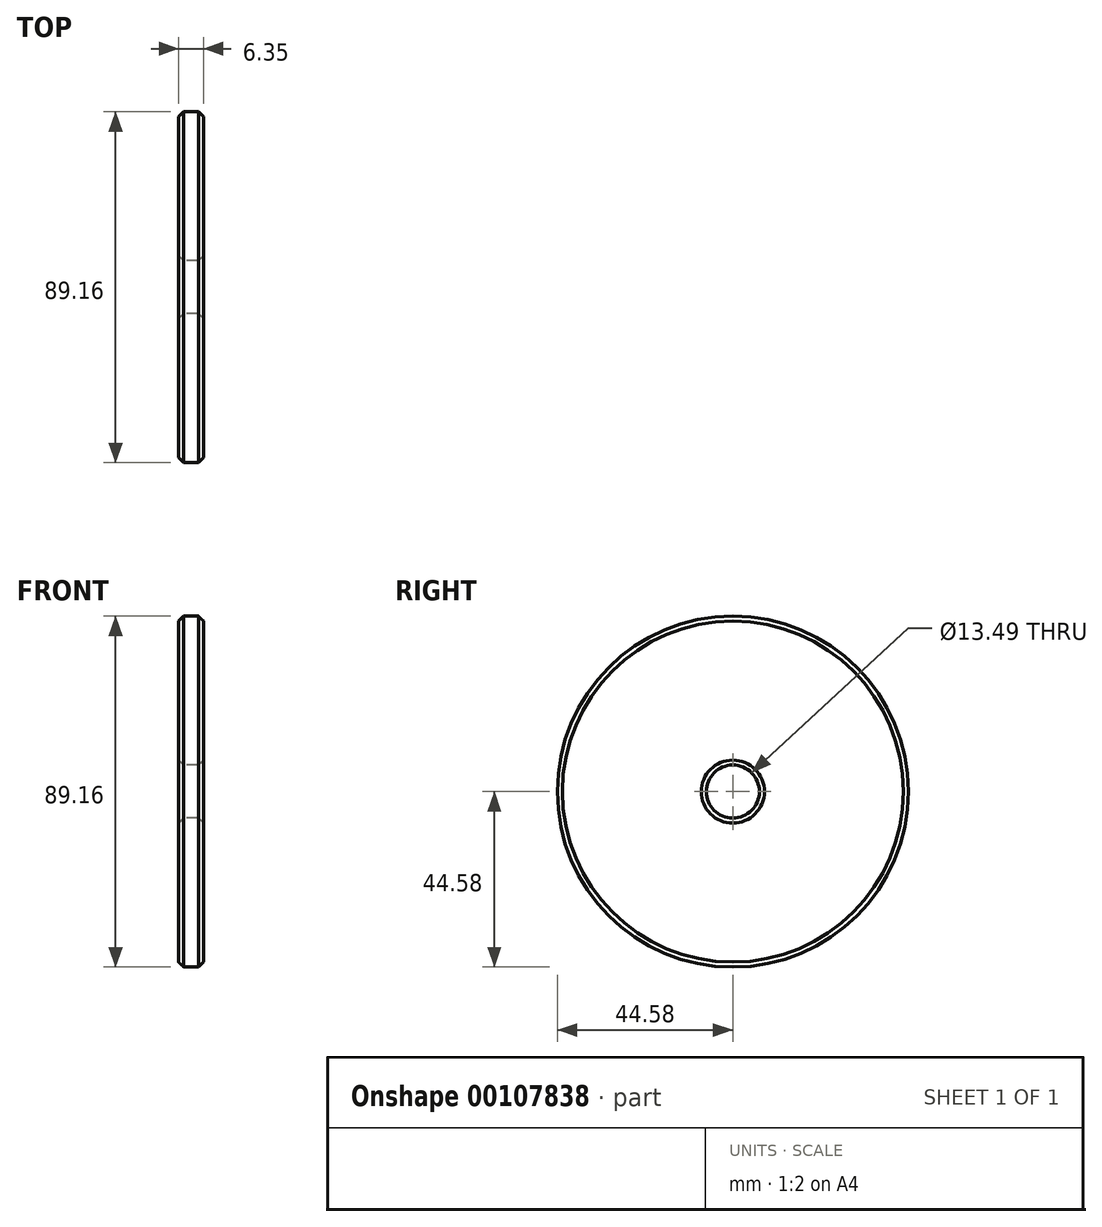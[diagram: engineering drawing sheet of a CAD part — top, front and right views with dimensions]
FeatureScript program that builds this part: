
annotation { "Feature Type Name" : "Feature", "Feature Type Description" : "" }
export const myFeature = defineFeature(function(context is Context, id is Id, definition is map)
    precondition{}
    {
        {
            var Q0;
            Q0=qCreatedBy(makeId("Top.planeOp"),FACE);
            var sketch = newSketch(context, id + "F0", { "sketchPlane" : qUnion([Q0])});
            skLineSegment(sketch, "E0", {"start": v(0, 6.75) * mm, "end": v(6.35, 6.75) * mm});
            skLineSegment(sketch, "E1", {"start": v(6.35, 6.75) * mm, "end": v(6.35, 44.58) * mm});
            skLineSegment(sketch, "E2", {"start": v(6.35, 44.58) * mm, "end": v(0, 44.58) * mm});
            skLineSegment(sketch, "E3", {"start": v(0, 44.58) * mm, "end": v(0, 6.75) * mm});
            skLineSegment(sketch, "E4", {"start": v(0, 0) * mm, "end": v(6.35, 0) * mm});
            skSolve(sketch);
        }
        {
            var Q0;
            Q0=makeQuery(id+"F0.imprint","IMPRINT",FACE,{"disambiguationData":[TD([[makeQuery(id+"F0.imprint","IMPRINT",EDGE,{"derivedFrom":sQuery(id+"F0.wireOp",EDGE,"E0")}),1.0]])]});
            var Q1;
            Q1=sQuery(id+"F0.wireOp",EDGE,"E4");
            revolve(context, id + "F1", {"entities" : qUnion([Q0]), "axis" : qUnion([Q1]), "revolveType" : RevolveType.FULL});
        }
        {
            var Q0;
            Q0=makeQuery(id+"F1.opRevolve","SWEPT_EDGE",EDGE,{"disambiguationData":[OSD([sQuery(id+"F0.wireOp",EDGE,"E1"),sQuery(id+"F0.wireOp",EDGE,"E2")])]});
            var Q1;
            Q1=makeQuery(id+"F1.opRevolve","SWEPT_EDGE",EDGE,{"disambiguationData":[OSD([sQuery(id+"F0.wireOp",EDGE,"E2"),sQuery(id+"F0.wireOp",EDGE,"E3")])]});
            var Q2;
            Q2=makeQuery(id+"F1.opRevolve","SWEPT_FACE",FACE,{"disambiguationData":[OSD([sQuery(id+"F0.wireOp",EDGE,"E1")])]});
            var Q3;
            Q3=makeQuery(id+"F1.opRevolve","SWEPT_EDGE",EDGE,{"disambiguationData":[OSD([sQuery(id+"F0.wireOp",EDGE,"E0"),sQuery(id+"F0.wireOp",EDGE,"E3")])]});
            chamfer(context, id + "F2", {"entities" : qUnion([Q0, Q1, Q2, Q3]), "width" : 1.27 * mm, "tangentPropagation" : true});
        }
    });
